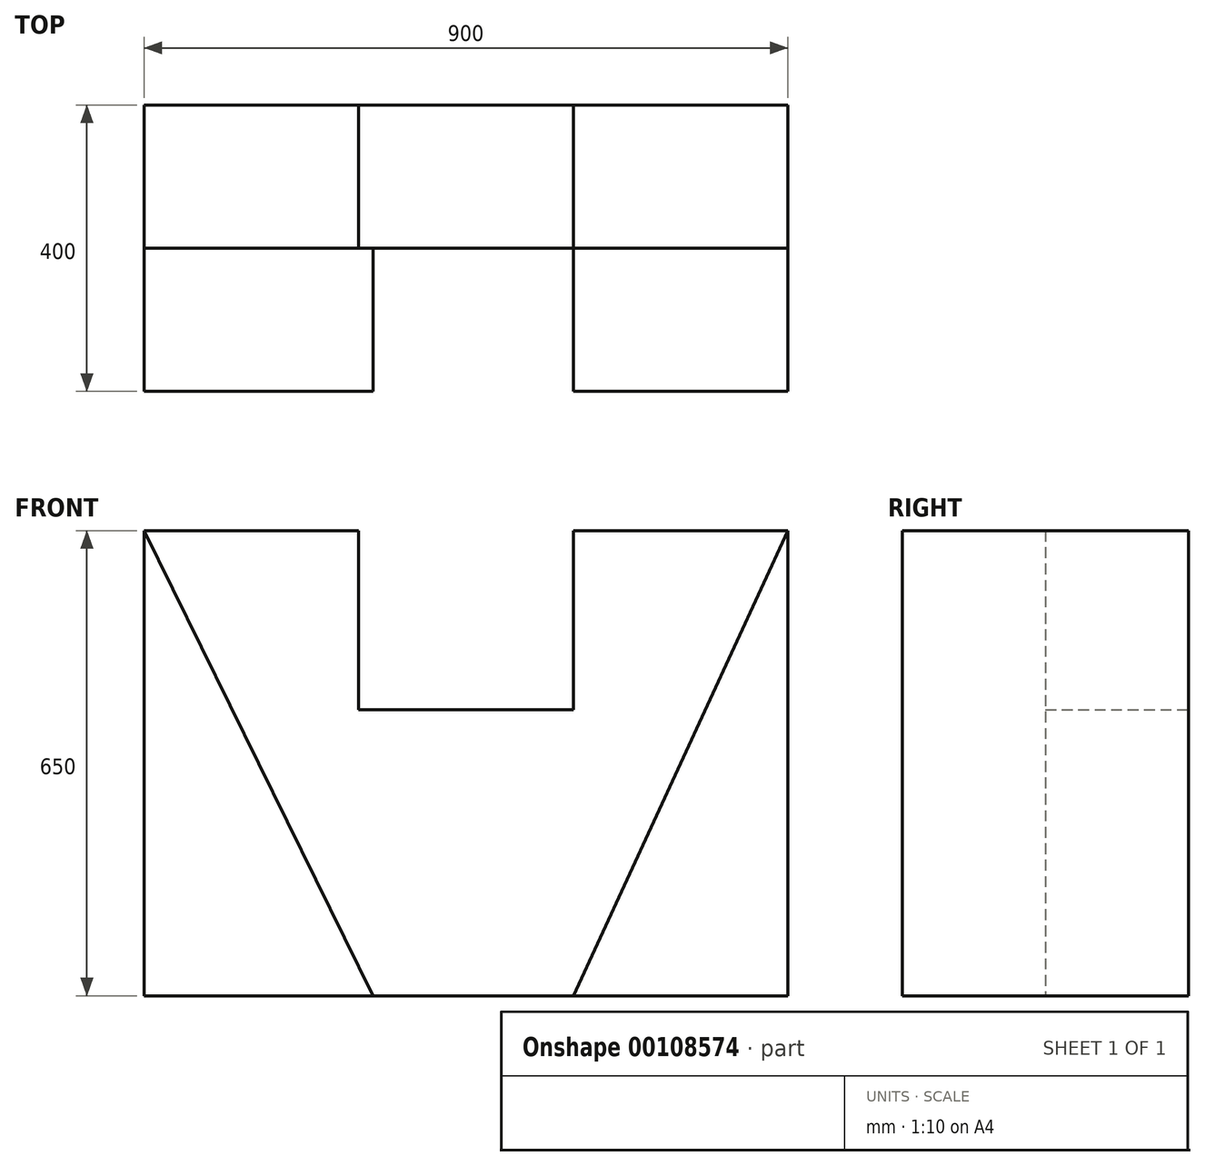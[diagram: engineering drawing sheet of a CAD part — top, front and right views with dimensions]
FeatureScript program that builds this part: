
annotation { "Feature Type Name" : "Feature", "Feature Type Description" : "" }
export const myFeature = defineFeature(function(context is Context, id is Id, definition is map)
    precondition{}
    {
        {
            var Q0;
            Q0=qCreatedBy(makeId("Front.planeOp"),FACE);
            var sketch = newSketch(context, id + "F0", { "sketchPlane" : qUnion([Q0])});
            skLineSegment(sketch, "E0.bottom", {"start": v(450, 325) * mm, "end": v(150, 325) * mm});
            skLineSegment(sketch, "E0.top", {"start": v(450, -325) * mm, "end": v(-450, -325) * mm});
            skLineSegment(sketch, "E0.left", {"start": v(450, 325) * mm, "end": v(450, -325) * mm});
            skLineSegment(sketch, "E0.right", {"start": v(-450, 325) * mm, "end": v(-450, -325) * mm});
            skPoint(sketch, "E0.middle", {"position": v(0, 0) * mm});
            skLineSegment(sketch, "E1.top", {"start": v(150, 75) * mm, "end": v(-150, 75) * mm});
            skLineSegment(sketch, "E1.left", {"start": v(150, 325) * mm, "end": v(150, 75) * mm});
            skLineSegment(sketch, "E1.right", {"start": v(-150, 325) * mm, "end": v(-150, 75) * mm});
            skPoint(sketch, "E1.middle", {"position": v(0, 325) * mm});
            skPoint(sketch, "E1.bottom.end.orphan", {"position": v(-150, 575) * mm});
            skPoint(sketch, "E2.orphan", {"position": v(150, 575) * mm});
            skLineSegment(sketch, "E3.trimOffspring", {"start": v(-150, 325) * mm, "end": v(-450, 325) * mm});
            skSolve(sketch);
        }
        {
            var Q0;
            Q0=makeQuery(id+"F0.imprint","IMPRINT",FACE,{"disambiguationData":[TD([[makeQuery(id+"F0.imprint","IMPRINT",EDGE,{"derivedFrom":sQuery(id+"F0.wireOp",EDGE,"E0.bottom")}),1.0]])]});
            extrude(context, id + "F1", {"entities" : qUnion([Q0]), "depth" : 200 * mm});
        }
        {
            var Q0;
            Q0=makeQuery(id+"F1.opExtrude","CAP_FACE",FACE,{"disambiguationData":[OSD([sQuery(id+"F0.wireOp",EDGE,"E0.bottom"),sQuery(id+"F0.wireOp",EDGE,"E0.top"),sQuery(id+"F0.wireOp",EDGE,"E0.left"),sQuery(id+"F0.wireOp",EDGE,"E0.right"),sQuery(id+"F0.wireOp",EDGE,"E1.top"),sQuery(id+"F0.wireOp",EDGE,"E1.left"),sQuery(id+"F0.wireOp",EDGE,"E1.right"),sQuery(id+"F0.wireOp",EDGE,"E3.trimOffspring")])],"isStart":false});
            var sketch = newSketch(context, id + "F2", { "sketchPlane" : qUnion([Q0])});
            skLineSegment(sketch, "E4", {"start": v(-450, 325) * mm, "end": v(-129.59, -325) * mm});
            skLineSegment(sketch, "E5", {"start": v(450, 325) * mm, "end": v(150, -325) * mm});
            skLineSegment(sketch, "E6", {"start": v(150, -325) * mm, "end": v(450, -325) * mm});
            skLineSegment(sketch, "E7", {"start": v(450, -325) * mm, "end": v(450, 325) * mm});
            skLineSegment(sketch, "E8", {"start": v(-450, 325) * mm, "end": v(-450, -325) * mm});
            skLineSegment(sketch, "E9", {"start": v(-429.59, -326.38) * mm, "end": v(-129.59, -325) * mm});
            skSolve(sketch);
        }
        {
            var Q0;
            {var subQ0=sQuery(id+"F2.wireOp",EDGE,"E4");Q0=makeQuery(id+"F2.imprint","IMPRINT",FACE,{"disambiguationData":[TD([[makeQuery(id+"F2.imprint","IMPRINT",EDGE,{"derivedFrom":subQ0}),-1.0]])]});}
            var Q1;
            Q1=makeQuery(id+"F2.imprint","IMPRINT",FACE,{"disambiguationData":[TD([[makeQuery(id+"F2.imprint","IMPRINT",EDGE,{"derivedFrom":sQuery(id+"F2.wireOp",EDGE,"E5")}),1.0]])]});
            extrude(context, id + "F3", {"entities" : qUnion([Q0, Q1]), "operationType" : NewBodyOperationType.ADD, "depth" : 200 * mm});
        }
    });
